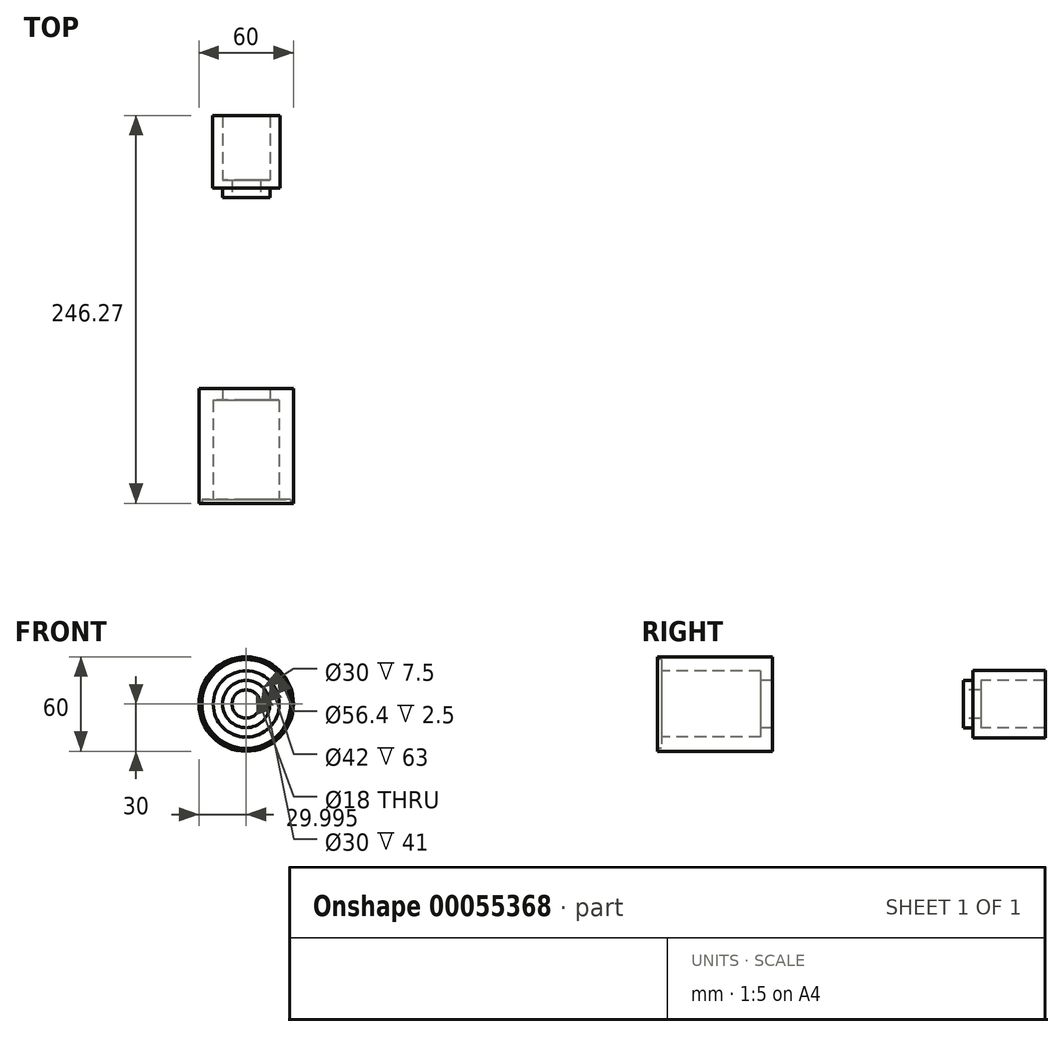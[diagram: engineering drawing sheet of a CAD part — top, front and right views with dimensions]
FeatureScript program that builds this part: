
annotation { "Feature Type Name" : "Feature", "Feature Type Description" : "" }
export const myFeature = defineFeature(function(context is Context, id is Id, definition is map)
    precondition{}
    {
        {
            var Q0;
            Q0=qCreatedBy(makeId("Front.planeOp"),FACE);
            var sketch = newSketch(context, id + "F0", { "sketchPlane" : qUnion([Q0])});
            skLineSegment(sketch, "E0", {"start": v(-60.61, 0) * mm, "end": v(43, 0) * mm, "construction": true});
            skLineSegment(sketch, "E1.0", {"start": v(-60.61, 30) * mm, "end": v(12.39, 30) * mm});
            skLineSegment(sketch, "E2.0", {"start": v(4.89, 15) * mm, "end": v(12.39, 15) * mm});
            skLineSegment(sketch, "E3.0", {"start": v(-58.11, 21) * mm, "end": v(4.89, 21) * mm});
            skLineSegment(sketch, "E4.0", {"start": v(-60.61, 28.2) * mm, "end": v(-58.11, 28.2) * mm});
            skLineSegment(sketch, "E5.0", {"start": v(12.39, 15) * mm, "end": v(12.39, 30) * mm});
            skLineSegment(sketch, "E6.0", {"start": v(4.89, 15) * mm, "end": v(4.89, 21) * mm});
            skLineSegment(sketch, "E7.trimOffspring", {"start": v(-60.61, 28.2) * mm, "end": v(-60.61, 30) * mm});
            skLineSegment(sketch, "E8.trimOffspring", {"start": v(-58.11, 21) * mm, "end": v(-58.11, 28.2) * mm});
            skLineSegment(sketch, "E9", {"start": v(133.66, 9) * mm, "end": v(133.66, 15) * mm});
            skLineSegment(sketch, "E10.trimOffspring", {"start": v(133.66, 0) * mm, "end": v(341.93, 0) * mm, "construction": true});
            skLineSegment(sketch, "E11.0", {"start": v(185.66, 15) * mm, "end": v(185.66, 21.5) * mm});
            skLineSegment(sketch, "E12.0", {"start": v(139.66, 21.5) * mm, "end": v(185.66, 21.5) * mm});
            skLineSegment(sketch, "E13.0", {"start": v(133.66, 15) * mm, "end": v(139.66, 15) * mm});
            skLineSegment(sketch, "E14.0", {"start": v(139.66, 15) * mm, "end": v(139.66, 21.5) * mm});
            skLineSegment(sketch, "E15.0", {"start": v(144.66, 9) * mm, "end": v(144.66, 15) * mm});
            skLineSegment(sketch, "E16.0", {"start": v(133.66, 9) * mm, "end": v(144.66, 9) * mm});
            skLineSegment(sketch, "E17.trimOffspring", {"start": v(144.66, 15) * mm, "end": v(185.66, 15) * mm});
            skLineSegment(sketch, "E18", {"start": v(43, 0) * mm, "end": v(43, 81.4) * mm, "construction": true});
            skSolve(sketch);
        }
        {
            var Q0;
            Q0=makeQuery(id+"F0.imprint","IMPRINT",FACE,{"disambiguationData":[TD([[makeQuery(id+"F0.imprint","IMPRINT",EDGE,{"derivedFrom":sQuery(id+"F0.wireOp",EDGE,"E1.0")}),-1.0]])]});
            var Q1;
            Q1=makeQuery(id+"F0.imprint","IMPRINT",FACE,{"disambiguationData":[TD([[makeQuery(id+"F0.imprint","IMPRINT",EDGE,{"derivedFrom":sQuery(id+"F0.wireOp",EDGE,"E9")}),-1.0]])]});
            var Q2;
            Q2=sQuery(id+"F0.wireOp",EDGE,"E0");
            revolve(context, id + "F1", {"entities" : qUnion([Q0, Q1]), "axis" : qUnion([Q2]), "revolveType" : RevolveType.FULL});
        }
        {
            var Q0;
            Q0=makeQuery(id+"F1.opRevolve","SWEPT_BODY",BODY,{"disambiguationData":[OSD([sQuery(id+"F0.wireOp",EDGE,"E1.0"),sQuery(id+"F0.wireOp",EDGE,"E2.0"),sQuery(id+"F0.wireOp",EDGE,"E3.0"),sQuery(id+"F0.wireOp",EDGE,"E4.0"),sQuery(id+"F0.wireOp",EDGE,"E5.0"),sQuery(id+"F0.wireOp",EDGE,"E6.0"),sQuery(id+"F0.wireOp",EDGE,"E7.trimOffspring"),sQuery(id+"F0.wireOp",EDGE,"E8.trimOffspring")])]});
            var Q1;
            Q1=makeQuery(id+"F1.opRevolve","SWEPT_BODY",BODY,{"disambiguationData":[OSD([sQuery(id+"F0.wireOp",EDGE,"E9"),sQuery(id+"F0.wireOp",EDGE,"E11.0"),sQuery(id+"F0.wireOp",EDGE,"E12.0"),sQuery(id+"F0.wireOp",EDGE,"E13.0"),sQuery(id+"F0.wireOp",EDGE,"E14.0"),sQuery(id+"F0.wireOp",EDGE,"E15.0"),sQuery(id+"F0.wireOp",EDGE,"E16.0"),sQuery(id+"F0.wireOp",EDGE,"E17.trimOffspring")])]});
            var Q2;
            Q2=sQuery(id+"F0.wireOp",EDGE,"E18");
            transform(context, id + "F2", {"entities" : qUnion([Q0, Q1]), "transformType" : TransformType.ROTATION, "transformAxis" : qUnion([Q2]), "angle" : 90 * degree, "makeCopy" : false});
        }
    });
